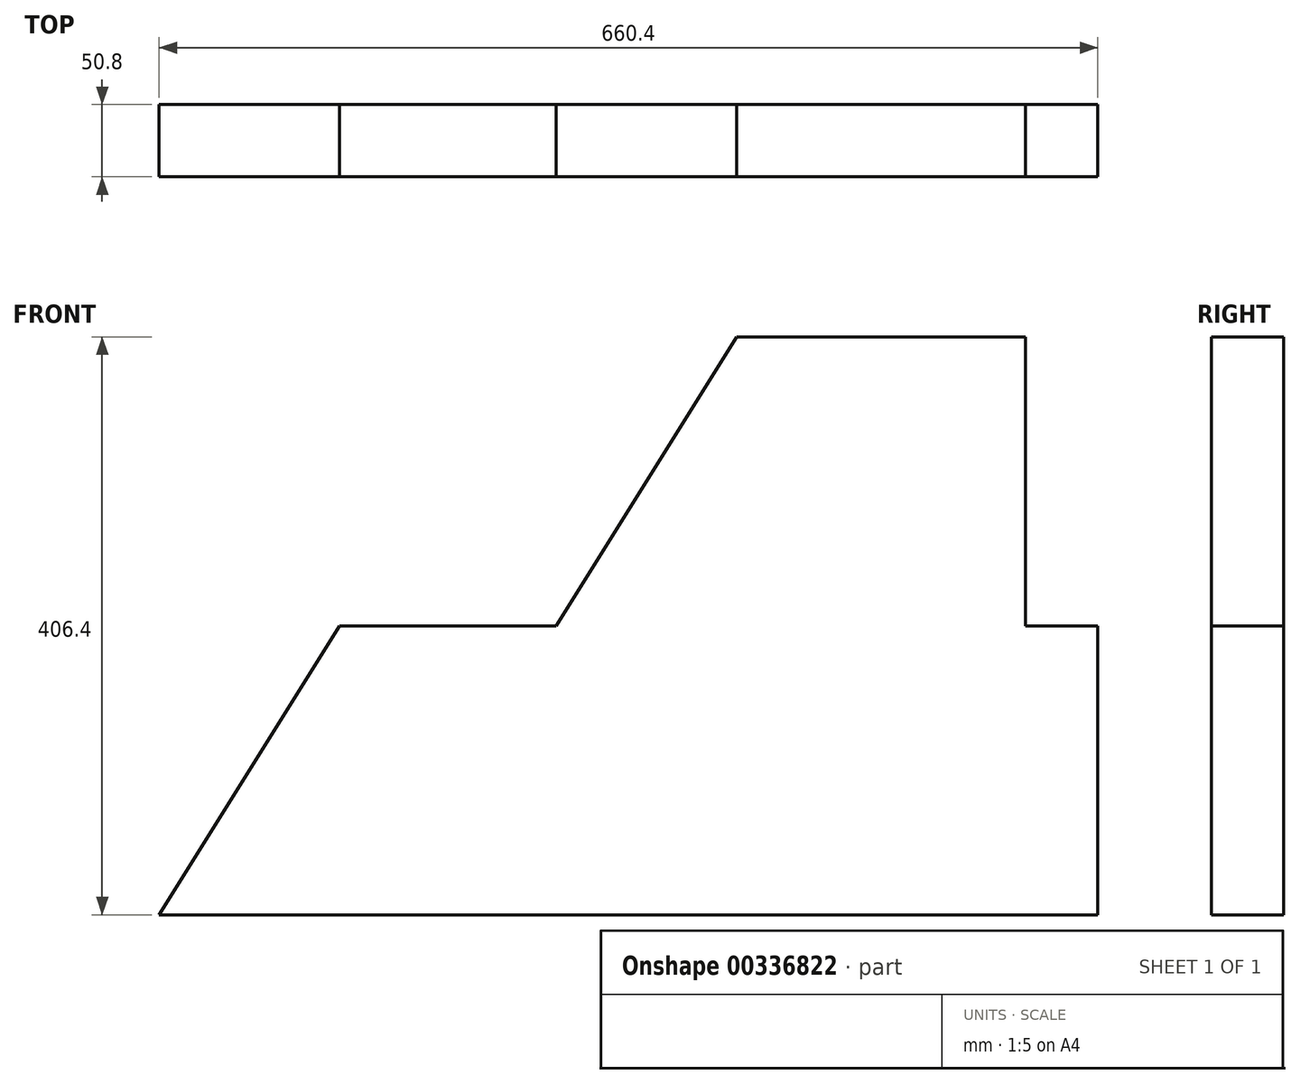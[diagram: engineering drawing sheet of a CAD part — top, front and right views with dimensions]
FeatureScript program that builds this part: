
annotation { "Feature Type Name" : "Feature", "Feature Type Description" : "" }
export const myFeature = defineFeature(function(context is Context, id is Id, definition is map)
    precondition{}
    {
        {
            var Q0;
            Q0=qCreatedBy(makeId("Front.planeOp"),FACE);
            var sketch = newSketch(context, id + "F0", { "sketchPlane" : qUnion([Q0])});
            skLineSegment(sketch, "E0", {"start": v(-114.49, 203.2) * mm, "end": v(88.71, 203.2) * mm});
            skLineSegment(sketch, "E1", {"start": v(88.71, 203.2) * mm, "end": v(88.71, 0) * mm});
            skLineSegment(sketch, "E2", {"start": v(88.71, 0) * mm, "end": v(139.51, 0) * mm});
            skLineSegment(sketch, "E3", {"start": v(139.51, 0) * mm, "end": v(139.51, -203.2) * mm});
            skLineSegment(sketch, "E4", {"start": v(139.51, -203.2) * mm, "end": v(-520.89, -203.2) * mm});
            skLineSegment(sketch, "E5", {"start": v(-114.49, 203.2) * mm, "end": v(-241.49, 0) * mm});
            skLineSegment(sketch, "E6", {"start": v(-241.49, 0) * mm, "end": v(-393.89, 0) * mm});
            skLineSegment(sketch, "E7", {"start": v(-393.89, 0) * mm, "end": v(-520.89, -203.2) * mm});
            skSolve(sketch);
        }
        {
            var Q0;
            Q0 = qSketchRegion(id + "F0", true);
            extrude(context, id + "F1", {"entities" : qUnion([Q0]), "depth" : 50.8 * mm});
        }
    });
